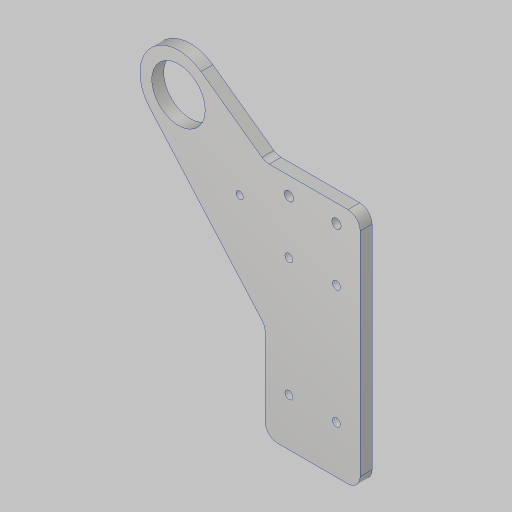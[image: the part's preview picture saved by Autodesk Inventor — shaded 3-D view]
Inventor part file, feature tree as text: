
AUTODESK INVENTOR PART (.ipt)
format: ipt  version: 2023.5 (Build 275446000, 446)  size: 315,392 bytes
history: native  units: in
note: dims shown in document units (in); Inventor stores cm internally (conversion verified against a paired STEP export)
features: sketch x4, hole x3, fillet x3, extrude x2, projected_geometry x2
ambient origin geometry x8: Origin, YZ Plane, XZ Plane, XY Plane, X Axis, Y Axis, Z Axis, Center Point
bodies: Solid1 (feature_tree)
feature tree (14):
  sketch  "Sketch1"  dims[d0=2.0in d1=15.0in]
  sketch  "Sketch2"  dims[d2=0.875in d3=17.0in]
  extrude  "Extrusion1"  Depth=2.0in
  hole  "Hole1"  [1 undecoded]
  hole  "Hole2"  [1 undecoded]
  fillet  "Fillet1"  Radius=1.0in
  hole  "Hole3"  [1 undecoded]
  fillet  "Fillet3"  Radius=0.5in
  extrude  "Extrusion2"  Depth=0.26in
  fillet  "Fillet2"  Radius=1.5in
  sketch  "Sketch3"  dims[d4=2.0in d5=17.0in d6=1.0in]
  projected_geometry  "Projected Loop1"
  sketch  "Sketch4"  dims[d7=0.2405in d8=2.4in d9=0.5in d10=3.6in d11=1.5in d12=1.5in d13=0.9in d14=3.7in d15=1.0in d16=3.4in d17=3.0in d20=2.0in d22=1.125in d23=4.297in d24=0.25in d25=2.0in d26=2.3622in d28=360.0deg d30=7.0in d31=2.0in d32=0.201in d33=1.0in d34=1.5in d35=1.0in d36=0.201in d37=1.0in d38=1.0in d39=2.5in d40=0.25in d41=0.0in d42=0.85in d43=0.201in d44=0.75in d45=0.385in d46=0.25in d47=0.5635in d48=1.0in d49=0.8108in d50=0.375in d51=0.171in d52=0.432in d53=0.385in d54=0.25in d55=0.5635in d56=1.0in d57=0.8108in d58=0.26in d59=1.825in d61=0.25in d62=0.25in d63=1.0in d64=0.125in d65=0.125in d66=0.125in d67=0.125in d68=0.125in d69=0.125in d70=1.0in d71=0.0in d72=0.13in d74=1.75in d75=0.875in d76=0.156in d77=0.38in d78=0.375in d79=0.25in d80=0.5635in d81=1.0in d82=0.8108in d83=0.125in d84=0.125in d87=3.0in d88=0.26in]
  projected_geometry  "Projected Loop2"
note: 3 required parameter values undecoded (feature->parameter linkage not recoverable at this tier; creation-order binding heuristic only, values carry confidence <= 0.55)
